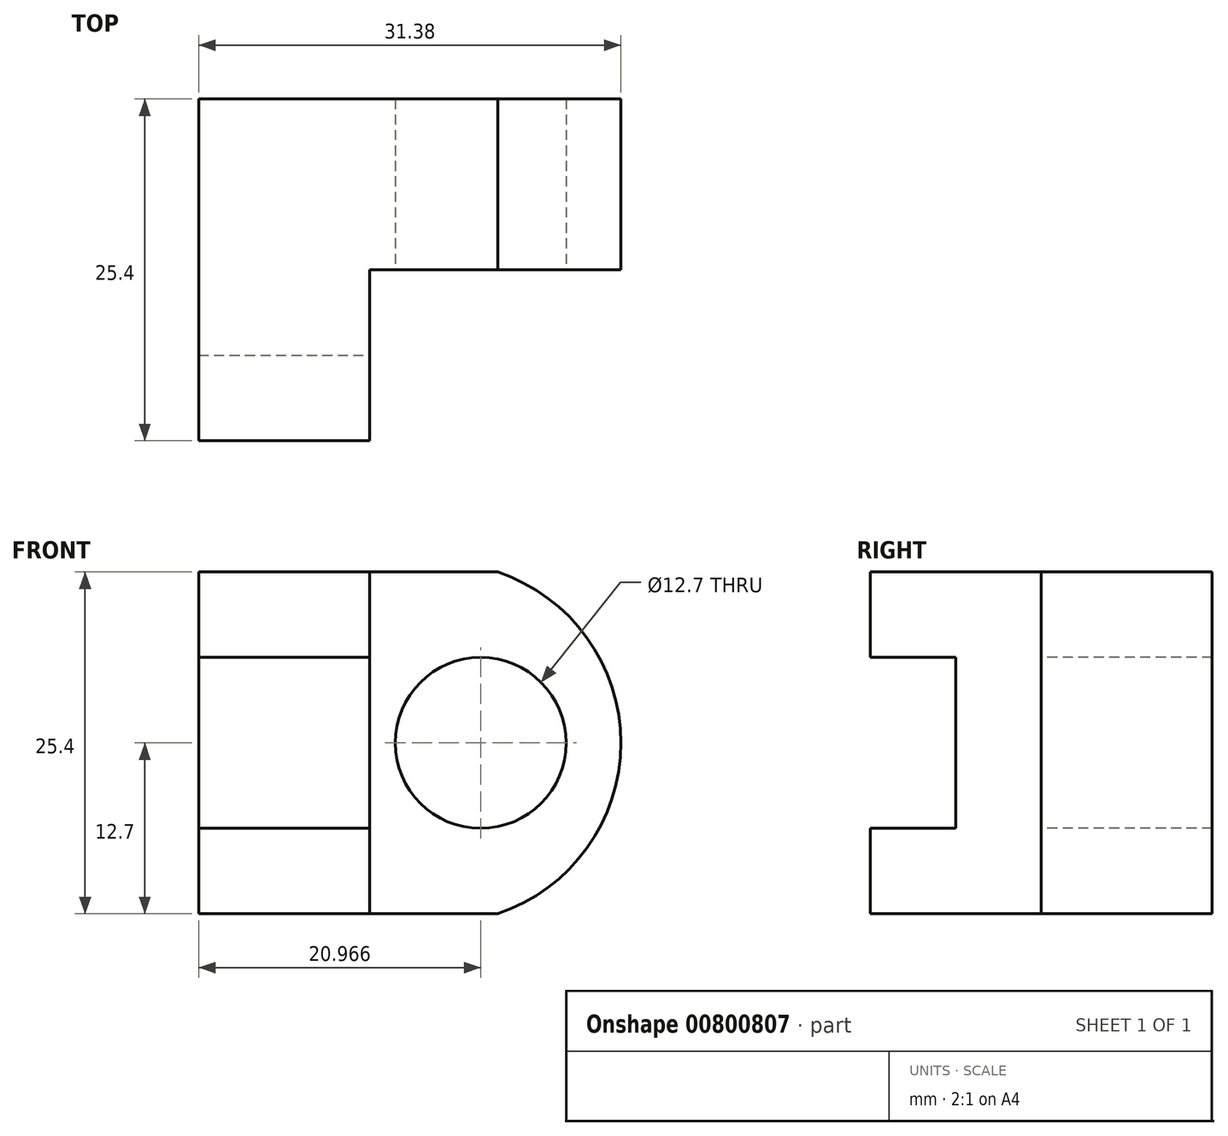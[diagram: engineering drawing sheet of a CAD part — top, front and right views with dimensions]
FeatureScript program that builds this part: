
annotation { "Feature Type Name" : "Feature", "Feature Type Description" : "" }
export const myFeature = defineFeature(function(context is Context, id is Id, definition is map)
    precondition{}
    {
        {
            var Q0;
            Q0=qCreatedBy(makeId("Front.planeOp"),FACE);
            var sketch = newSketch(context, id + "F0", { "sketchPlane" : qUnion([Q0])});
            skLineSegment(sketch, "E0", {"start": v(0, 0) * mm, "end": v(0, 25.4) * mm});
            skLineSegment(sketch, "E1", {"start": v(0, 25.4) * mm, "end": v(31.75, 25.4) * mm});
            skLineSegment(sketch, "E2", {"start": v(31.75, 25.4) * mm, "end": v(31.75, 0) * mm});
            skLineSegment(sketch, "E3", {"start": v(31.75, 0) * mm, "end": v(0, 0) * mm});
            skSolve(sketch);
        }
        {
            var Q0;
            Q0=makeQuery(id+"F0.imprint","IMPRINT",FACE,{"disambiguationData":[TD([[makeQuery(id+"F0.imprint","IMPRINT",EDGE,{"derivedFrom":sQuery(id+"F0.wireOp",EDGE,"E0")}),-1.0]])]});
            extrude(context, id + "F1", {"entities" : qUnion([Q0]), "depth" : 25.4 * mm, "offsetDistance" : 25.4 * mm});
        }
        {
            var Q0;
            Q0=makeQuery(id+"F1.opExtrude","SWEPT_FACE",FACE,{"disambiguationData":[OSD([sQuery(id+"F0.wireOp",EDGE,"E2")])]});
            var sketch = newSketch(context, id + "F2", { "sketchPlane" : qUnion([Q0])});
            skLineSegment(sketch, "E4", {"start": v(-25.4, 25.4) * mm, "end": v(-12.7, 25.4) * mm});
            skLineSegment(sketch, "E5", {"start": v(-12.7, 25.4) * mm, "end": v(-12.7, 0) * mm});
            skLineSegment(sketch, "E6", {"start": v(-12.7, 0) * mm, "end": v(-25.4, 0) * mm});
            skLineSegment(sketch, "E7", {"start": v(-25.4, 0) * mm, "end": v(-25.4, 6.35) * mm});
            skLineSegment(sketch, "E8", {"start": v(-25.4, 6.35) * mm, "end": v(-19.05, 6.35) * mm});
            skLineSegment(sketch, "E9", {"start": v(-19.05, 6.35) * mm, "end": v(-19.05, 19.05) * mm});
            skLineSegment(sketch, "E10", {"start": v(-19.05, 19.05) * mm, "end": v(-25.4, 19.05) * mm});
            skLineSegment(sketch, "E11", {"start": v(-25.4, 19.05) * mm, "end": v(-25.4, 25.4) * mm});
            skSolve(sketch);
        }
        {
            var Q0;
            {var subQ0=sQuery(id+"F2.wireOp",EDGE,"E8");Q0=makeQuery(id+"F2.imprint","IMPRINT",FACE,{"disambiguationData":[TD([[makeQuery(id+"F2.imprint","IMPRINT",EDGE,{"derivedFrom":subQ0}),1.0]])]});}
            extrude(context, id + "F3", {"entities" : qUnion([Q0]), "operationType" : NewBodyOperationType.REMOVE, "oppositeDirection" : true, "depth" : 25.4 * mm, "offsetDistance" : 25.4 * mm});
        }
        {
            var Q0;
            Q0=makeQuery(id+"F3.boolean.opBoolean","COPY",FACE,{"derivedFrom":makeQuery(id+"F3.opExtrude","CAP_FACE",FACE,{"disambiguationData":[OSD([sQuery(id+"F0.wireOp",EDGE,"E2"),sQuery(id+"F2.wireOp",EDGE,"E8"),sQuery(id+"F2.wireOp",EDGE,"E9"),sQuery(id+"F2.wireOp",EDGE,"E10")])],"isStart":false})});
            extrude(context, id + "F4", {"entities" : qUnion([Q0]), "operationType" : NewBodyOperationType.REMOVE, "oppositeDirection" : true, "depth" : 25.4 * mm, "offsetDistance" : 25.4 * mm});
        }
        {
            var Q0;
            Q0=makeQuery(id+"F1.opExtrude","SWEPT_FACE",FACE,{"disambiguationData":[OSD([sQuery(id+"F0.wireOp",EDGE,"E1")])]});
            var sketch = newSketch(context, id + "F5", { "sketchPlane" : qUnion([Q0])});
            skLineSegment(sketch, "E12", {"start": v(0, -25.4) * mm, "end": v(12.7, -25.4) * mm});
            skLineSegment(sketch, "E13", {"start": v(12.7, -25.4) * mm, "end": v(12.7, -12.7) * mm});
            skLineSegment(sketch, "E14", {"start": v(12.7, -12.7) * mm, "end": v(31.75, -12.7) * mm});
            skSolve(sketch);
        }
        {
            var Q0;
            {var subQ0=sQuery(id+"F5.wireOp",EDGE,"E13");Q0=makeQuery(id+"F5.imprint","IMPRINT",FACE,{"disambiguationData":[TD([[makeQuery(id+"F5.imprint","IMPRINT",EDGE,{"derivedFrom":subQ0}),-1.0]])]});}
            extrude(context, id + "F6", {"entities" : qUnion([Q0]), "operationType" : NewBodyOperationType.REMOVE, "oppositeDirection" : true, "depth" : 25.4 * mm, "offsetDistance" : 25.4 * mm});
        }
        {
            var Q0;
            Q0=makeQuery(id+"F6.boolean.opBoolean","COPY",FACE,{"derivedFrom":makeQuery(id+"F6.opExtrude","SWEPT_FACE",FACE,{"disambiguationData":[OSD([sQuery(id+"F5.wireOp",EDGE,"E14")])]})});
            var sketch = newSketch(context, id + "F7", { "sketchPlane" : qUnion([Q0])});
            skLineSegment(sketch, "E15", {"start": v(12.7, 12.7) * mm, "end": v(20.97, 12.7) * mm, "construction": true});
            skLineSegment(sketch, "E16", {"start": v(20.97, 12.7) * mm, "end": v(20.97, 25.4) * mm, "construction": true});
            skCircle(sketch, "E17", {"center": v(20.97, 12.7) * mm, "radius": 6.35 * mm});
            skSolve(sketch);
        }
        {
            var Q0;
            Q0=makeQuery(id+"F7.imprint","IMPRINT",FACE,{"disambiguationData":[TD([[makeQuery(id+"F7.imprint","IMPRINT",EDGE,{"derivedFrom":sQuery(id+"F7.wireOp",EDGE,"E17")}),1.0]])]});
            extrude(context, id + "F8", {"entities" : qUnion([Q0]), "operationType" : NewBodyOperationType.REMOVE, "endBound" : BoundingType.UP_TO_NEXT, "oppositeDirection" : true, "depth" : 25.4 * mm, "offsetDistance" : 25.4 * mm});
        }
        {
            var Q0;
            Q0=makeQuery(id+"F6.boolean.opBoolean","COPY",FACE,{"derivedFrom":makeQuery(id+"F6.opExtrude","SWEPT_FACE",FACE,{"disambiguationData":[OSD([sQuery(id+"F5.wireOp",EDGE,"E14")])]})});
            var sketch = newSketch(context, id + "F9", { "sketchPlane" : qUnion([Q0])});
            skArc(sketch, "E18", {"start": v(22.23, 0) * mm, "mid": v(31.38, 12.7) * mm, "end": v(22.23, 25.4) * mm});
            skSolve(sketch);
        }
        {
            var Q0;
            {var subQ0=sQuery(id+"F9.wireOp",EDGE,"E18");Q0=makeQuery(id+"F9.imprint","IMPRINT",FACE,{"disambiguationData":[TD([[makeQuery(id+"F9.imprint","IMPRINT",EDGE,{"derivedFrom":subQ0}),-1.0]])]});}
            extrude(context, id + "F10", {"entities" : qUnion([Q0]), "operationType" : NewBodyOperationType.REMOVE, "oppositeDirection" : true, "depth" : 25.4 * mm, "offsetDistance" : 25.4 * mm});
        }
    });
